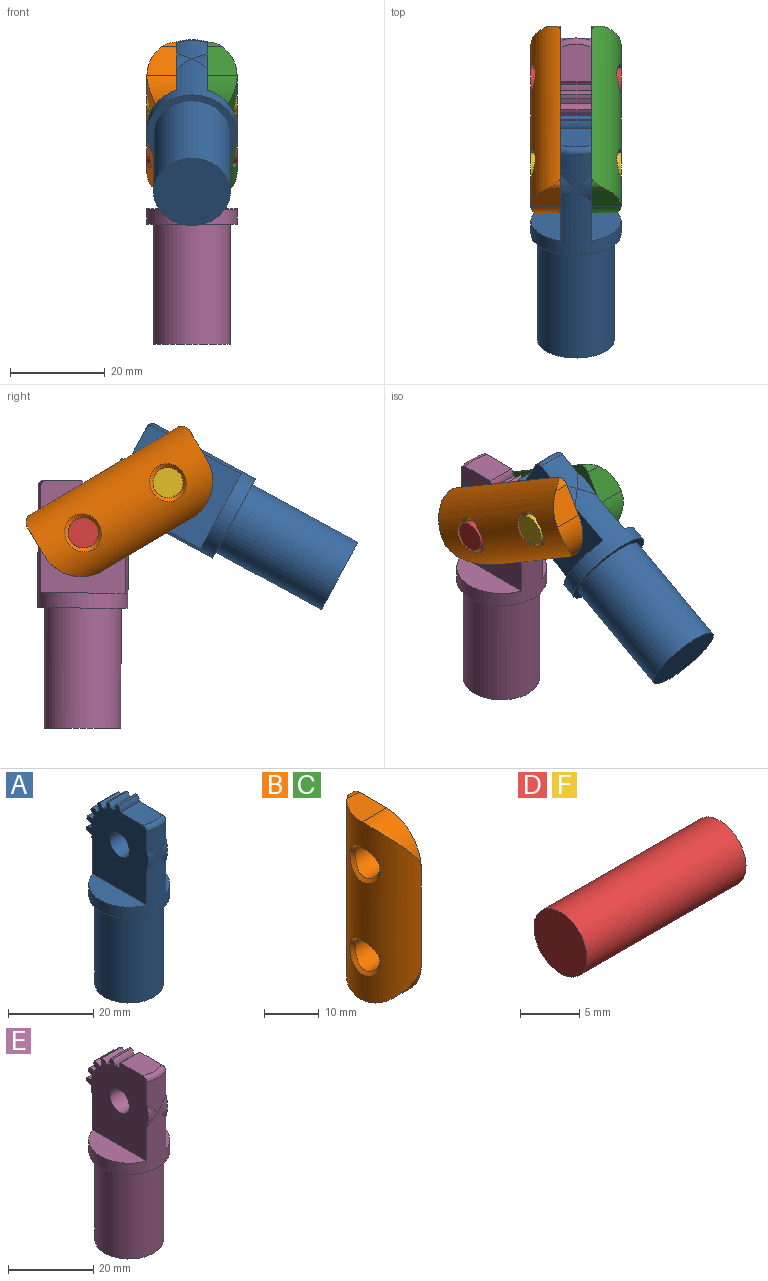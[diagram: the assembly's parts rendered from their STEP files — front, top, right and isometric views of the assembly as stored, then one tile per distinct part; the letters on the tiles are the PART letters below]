
ASSEMBLY  parts=6 mates=10
PART A: 39 faces, bbox 19.1x21.4x52.4 mm
  f0: cylinder r=9.53mm len=8.26mm, axis (0,0,-1), area 43.1mm2, adj f7,f8,f34,f35,f38
  f1: plane 8.06x6.35mm, normal (0,0,1), area 49.9mm2, adj f7,f8,f24,f38
  f2: cylinder r=9.53mm len=6.35mm, axis (1,0,0), area 8.7mm2, adj f7,f8,f16,f30
  f3: cylinder r=9.53mm len=6.35mm, axis (1,0,0), area 8.7mm2, adj f7,f8,f15,f19
  f4: cylinder r=9.53mm len=6.35mm, axis (1,0,0), area 8.7mm2, adj f7,f8,f18,f22
  f5: cylinder r=9.53mm len=6.35mm, axis (1,0,0), area 8.7mm2, adj f7,f8,f21,f25
  f6: cylinder r=9.53mm len=19.05mm, axis (0,0,-1), area 331.7mm2, adj f7,f8,f9,f12,f13,f31,f32,f33
  f7: plane 23.81x20.63mm, normal (1,0,0), area 369.5mm2, adj f0,f1,f2,f3,f4,f5,f6,f12
  f8: plane 23.81x20.63mm, normal (-1,0,0), area 369.5mm2, adj f0,f1,f2,f3,f4,f5,f6,f13
  f9: plane 19.05x19.05mm, normal (0,0,-1), area 79.1mm2, adj f6,f10
  f10: cylinder r=8.1mm len=25.4mm, axis (0,0,1), area 1292.1mm2, adj f9,f11
  f11: plane 16.19x16.19mm, normal (0,0,-1), area 205.9mm2, adj f10
  f12: plane 17.96x6.35mm, normal (0,0,1), area 83.2mm2, adj f6,f7
  f13: plane 17.96x6.35mm, normal (0,0,1), area 83.2mm2, adj f6,f8
  f14: plane 6.35x0.7mm, normal (0,0.85,0.53), area 5.2mm2, adj f7,f8,f15,f16
  f15: cylinder r=3.17mm len=6.35mm, axis (1,0,0), area 10.7mm2, adj f3,f7,f8,f14
  f16: cylinder r=3.17mm len=6.35mm, axis (1,0,0), area 10.7mm2, adj f2,f7,f8,f14
  f17: plane 6.35x0.63mm, normal (0,0.64,0.77), area 5.2mm2, adj f7,f8,f18,f19
  f18: cylinder r=3.17mm len=6.35mm, axis (1,0,0), area 10.7mm2, adj f4,f7,f8,f17
  f19: cylinder r=3.17mm len=6.35mm, axis (1,0,0), area 10.7mm2, adj f3,f7,f8,f17
  f20: plane 6.35x0.77mm, normal (0,0.37,0.93), area 5.2mm2, adj f7,f8,f21,f22
  f21: cylinder r=3.17mm len=6.35mm, axis (1,0,0), area 10.7mm2, adj f5,f7,f8,f20
  f22: cylinder r=3.17mm len=6.35mm, axis (1,0,0), area 10.7mm2, adj f4,f7,f8,f20
  f23: plane 6.35x0.82mm, normal (0,0.07,1), area 5.2mm2, adj f7,f8,f24,f25
  f24: cylinder r=3.17mm len=6.35mm, axis (1,0,0), area 10.7mm2, adj f1,f7,f8,f23
  f25: cylinder r=3.17mm len=6.35mm, axis (1,0,0), area 10.7mm2, adj f5,f7,f8,f23
  f26: plane 6.35x0.82mm, normal (0,1,-0.07), area 5.2mm2, adj f7,f8,f27,f33
  f27: cylinder r=3.17mm len=6.35mm, axis (1,0,0), area 10.7mm2, adj f7,f8,f26,f36
  f28: plane 6.35x0.8mm, normal (0,0.97,0.25), area 5.2mm2, adj f7,f8,f29,f30
  f29: cylinder r=3.17mm len=6.35mm, axis (1,0,0), area 10.7mm2, adj f7,f8,f28,f36
  f30: cylinder r=3.17mm len=6.35mm, axis (1,0,0), area 10.7mm2, adj f2,f7,f8,f28
  f31: cylinder r=9.53mm len=1.74mm, axis (1,0,0), area 1.6mm2, adj f6,f7,f33
  f32: cylinder r=9.53mm len=1.74mm, axis (1,0,0), area 1.6mm2, adj f6,f8,f33
  f33: cylinder r=3.17mm len=6.35mm, axis (1,0,0), area 10.5mm2, adj f6,f7,f8,f26,f31,f32
  f34: cylinder r=9.53mm len=6.35mm, axis (1,0,0), area 10.2mm2, adj f0,f6,f8
  f35: cylinder r=9.53mm len=6.35mm, axis (1,0,0), area 10.2mm2, adj f0,f6,f7
  f36: cylinder r=9.53mm len=6.35mm, axis (1,0,0), area 8.7mm2, adj f7,f8,f27,f29
  f37: cylinder r=3.17mm len=6.35mm, axis (1,0,0), area 126.7mm2, adj f7,f8
  f38: torus R=8.26mm, axis (0,0,1), area 12.9mm2, adj f0,f1,f7,f8
PART B: 12 faces, bbox 6.4x18x39.9 mm
  f0: plane 39.88x17.98mm, normal (1,0,0), area 617.4mm2, adj f1,f2,f3,f4,f5,f6,f7,f8
  f1: cylinder r=9.53mm len=39.88mm, axis (0,0,1), area 769.3mm2, adj f0,f2,f3,f4,f5,f6,f7,f10
  f2: plane 7.08x6.36mm, normal (0,0,-1), area 38.2mm2, adj f0,f1,f5,f7
  f3: plane 7.08x6.36mm, normal (0,0,1), area 38.2mm2, adj f0,f1,f4,f6
  f4: cylinder r=8.99mm len=8.99mm, axis (1,0,0), area 44.9mm2, adj f0,f1,f3
  f5: cylinder r=1.91mm len=3.2mm, axis (1,0,0), area 4.8mm2, adj f0,f1,f2
  f6: cylinder r=1.91mm len=3.2mm, axis (1,0,0), area 4.8mm2, adj f0,f1,f3
  f7: cylinder r=8.99mm len=8.99mm, axis (1,0,0), area 44.9mm2, adj f0,f1,f2
  f8: cylinder r=3.17mm len=6.35mm, axis (1,0,0), area 114.1mm2, adj f0,f11
  f9: cylinder r=3.17mm len=6.35mm, axis (1,0,0), area 114.1mm2, adj f0,f10
  f10: bspline ~8.17x7.62mm, area 22.4mm2, adj f1,f9
  f11: bspline ~8.17x7.62mm, area 22.4mm2, adj f1,f8
PART C: same geometry as B
PART D: 3 faces, bbox 19.1x6.4x6.4 mm
  f0: cylinder r=3.17mm len=19.05mm, axis (-1,0,0), area 380mm2, adj f1,f2
  f1: plane 6.35x6.35mm, normal (1,0,0), area 31.7mm2, adj f0
  f2: plane 6.35x6.35mm, normal (-1,0,0), area 31.7mm2, adj f0
PART E: 37 faces, bbox 19.1x21.4x52.4 mm
  f0: cylinder r=9.53mm len=9.84mm, axis (0,0,-1), area 53.4mm2, adj f6,f7,f31,f32,f36
  f1: cylinder r=9.53mm len=6.35mm, axis (1,0,0), area 8.7mm2, adj f6,f7,f18,f23
  f2: cylinder r=9.53mm len=6.35mm, axis (1,0,0), area 8.7mm2, adj f6,f7,f22,f26
  f3: cylinder r=9.53mm len=6.35mm, axis (1,0,0), area 8.7mm2, adj f6,f7,f25,f29
  f4: cylinder r=9.53mm len=6.35mm, axis (1,0,0), area 8.7mm2, adj f6,f7,f28,f30
  f5: cylinder r=9.53mm len=19.05mm, axis (0,0,-1), area 333.8mm2, adj f6,f7,f8,f11,f12,f15,f16,f17
  f6: plane 23.81x20.63mm, normal (1,0,0), area 381.5mm2, adj f0,f1,f2,f3,f4,f5,f11,f13
  f7: plane 23.81x20.63mm, normal (-1,0,0), area 381.5mm2, adj f0,f1,f2,f3,f4,f5,f12,f13
  f8: plane 19.05x19.05mm, normal (0,0,-1), area 79.1mm2, adj f5,f9
  f9: cylinder r=8.1mm len=25.4mm, axis (0,0,1), area 1292.1mm2, adj f8,f10
  f10: plane 16.19x16.19mm, normal (0,0,-1), area 205.9mm2, adj f9
  f11: plane 17.96x6.35mm, normal (0,0,1), area 83.2mm2, adj f5,f6
  f12: plane 17.96x6.35mm, normal (0,0,1), area 83.2mm2, adj f5,f7
  f13: plane 6.35x0.77mm, normal (0,0.93,0.37), area 5.2mm2, adj f6,f7,f18,f19
  f14: plane 6.35x0.82mm, normal (0,1,0.07), area 5.2mm2, adj f6,f7,f15,f20
  f15: cylinder r=3.17mm len=6.35mm, axis (1,0,0), area 10.7mm2, adj f5,f6,f7,f14,f16,f17
  f16: cylinder r=9.53mm len=2.98mm, axis (1,0,0), area 4.5mm2, adj f5,f6,f15
  f17: cylinder r=9.53mm len=2.98mm, axis (1,0,0), area 4.5mm2, adj f5,f7,f15
  f18: cylinder r=3.17mm len=6.35mm, axis (1,0,0), area 10.7mm2, adj f1,f6,f7,f13
  f19: cylinder r=3.17mm len=6.35mm, axis (1,0,0), area 10.7mm2, adj f6,f7,f13,f33
  f20: cylinder r=3.17mm len=6.35mm, axis (1,0,0), area 10.7mm2, adj f6,f7,f14,f33
  f21: plane 6.35x0.63mm, normal (0,0.77,0.64), area 5.2mm2, adj f6,f7,f22,f23
  f22: cylinder r=3.17mm len=6.35mm, axis (1,0,0), area 10.7mm2, adj f2,f6,f7,f21
  f23: cylinder r=3.17mm len=6.35mm, axis (1,0,0), area 10.7mm2, adj f1,f6,f7,f21
  f24: plane 6.35x0.7mm, normal (0,0.53,0.85), area 5.2mm2, adj f6,f7,f25,f26
  f25: cylinder r=3.17mm len=6.35mm, axis (1,0,0), area 10.7mm2, adj f3,f6,f7,f24
  f26: cylinder r=3.17mm len=6.35mm, axis (1,0,0), area 10.7mm2, adj f2,f6,f7,f24
  f27: plane 6.35x0.8mm, normal (0,0.25,0.97), area 5.2mm2, adj f6,f7,f28,f29
  f28: cylinder r=3.17mm len=6.35mm, axis (1,0,0), area 10.7mm2, adj f4,f6,f7,f27
  f29: cylinder r=3.17mm len=6.35mm, axis (1,0,0), area 10.7mm2, adj f3,f6,f7,f27
  f30: cylinder r=3.17mm len=6.35mm, axis (1,0,0), area 10.7mm2, adj f4,f6,f7,f35
  f31: cylinder r=9.53mm len=6.35mm, axis (1,0,0), area 10.3mm2, adj f0,f5,f7
  f32: cylinder r=9.53mm len=6.35mm, axis (1,0,0), area 10.3mm2, adj f0,f5,f6
  f33: cylinder r=9.53mm len=6.35mm, axis (1,0,0), area 8.7mm2, adj f6,f7,f19,f20
  f34: cylinder r=3.17mm len=6.35mm, axis (1,0,0), area 126.7mm2, adj f6,f7
  f35: plane 7.94x6.35mm, normal (0,0,1), area 49.1mm2, adj f6,f7,f30,f36
  f36: torus R=8.26mm, axis (0,0,1), area 12.9mm2, adj f0,f6,f7,f35
PART F: same geometry as D
PLACE A rot(axis=(-1,0,0),61.5deg) t=(-65.75,46.14,99.92)mm
PLACE B rot(axis=(1,0,0),59.4deg) t=(-65.75,69.05,102.19)mm
PLACE C rot(axis=(0,-0.87,-0.5),180deg) t=(-65.75,69.05,102.19)mm
PLACE D rot(axis=(1,0,0),149.4deg) t=(-75.27,78.01,96.88)mm
PLACE E rot(axis=(0,0,-1),180deg) t=(-65.75,78.07,81.01)mm
PLACE F rot(axis=(0,0.96,-0.26),180deg) t=(-56.22,60.09,107.5)mm
MATE planar A.f31 <-> B.f4  axis (-1,0,0) through (-68.92,60.09,107.5)mm
MATE revolute F.f0 <-> A.f2  axis (1,0,0) through (-65.75,60.09,107.5)mm
MATE planar A.f2 <-> C.f7  axis (1,0,0) through (-62.57,60.09,107.5)mm
MATE slider C.f8 <-> D.f0  axis (-1,0,0) through (-62.57,78.01,96.88)mm
MATE revolute E.f1 <-> D.f0  axis (-1,0,0) through (-65.75,78.01,96.88)mm
MATE slider C.f9 <-> F.f0  axis (-1,0,0) through (-62.57,60.09,107.5)mm
MATE slider B.f9 <-> D.f0  axis (1,0,0) through (-68.92,78.01,96.88)mm
MATE planar C.f8 <-> E.f1  axis (-1,0,0) through (-62.57,78.01,96.88)mm
MATE planar B.f9 <-> E.f1  axis (1,0,0) through (-68.92,78.01,96.88)mm
MATE slider B.f8 <-> F.f0  axis (1,0,0) through (-68.92,60.09,107.5)mm
